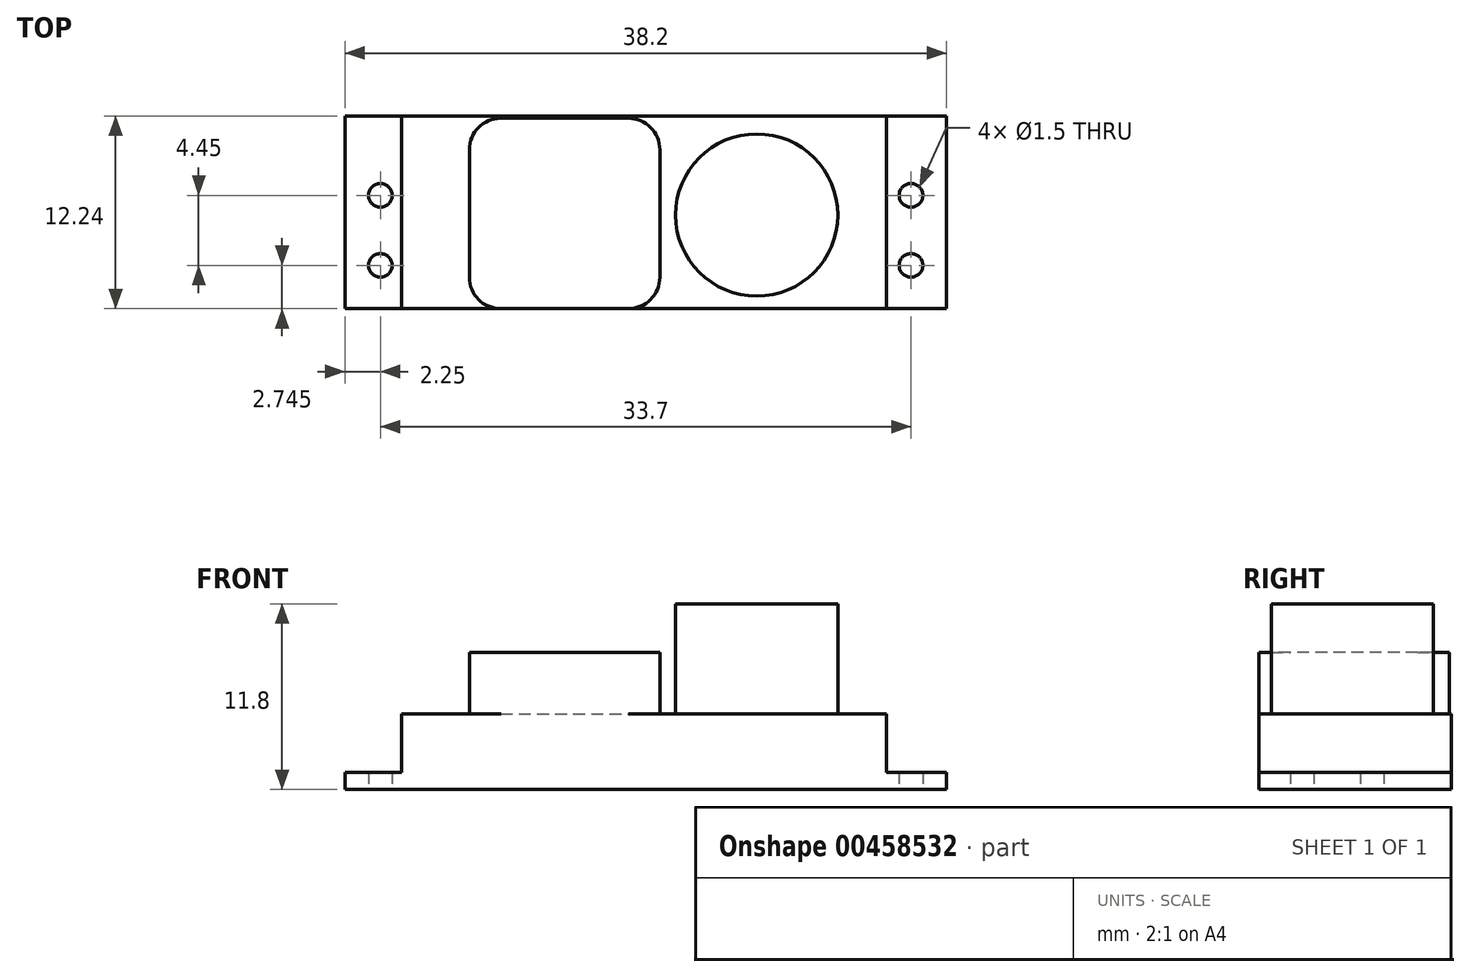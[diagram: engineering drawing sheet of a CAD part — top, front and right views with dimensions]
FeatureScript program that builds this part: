
annotation { "Feature Type Name" : "Feature", "Feature Type Description" : "" }
export const myFeature = defineFeature(function(context is Context, id is Id, definition is map)
    precondition{}
    {
        {
            var Q0;
            Q0=qCreatedBy(makeId("Top.planeOp"),FACE);
            var sketch = newSketch(context, id + "F0", { "sketchPlane" : qUnion([Q0])});
            skLineSegment(sketch, "E0.bottom", {"start": v(-19.1, 6.12) * mm, "end": v(19.1, 6.12) * mm});
            skLineSegment(sketch, "E0.top", {"start": v(-19.1, -6.12) * mm, "end": v(19.1, -6.12) * mm});
            skLineSegment(sketch, "E0.left", {"start": v(-19.1, 6.12) * mm, "end": v(-19.1, -6.12) * mm});
            skLineSegment(sketch, "E0.right", {"start": v(19.1, 6.12) * mm, "end": v(19.1, -6.12) * mm});
            skPoint(sketch, "E0.middle", {"position": v(0, 0) * mm});
            skCircle(sketch, "E1", {"center": v(-16.85, 1.08) * mm, "radius": 0.75 * mm});
            skCircle(sketch, "E2", {"center": v(-16.85, -3.38) * mm, "radius": 0.75 * mm});
            skCircle(sketch, "E3", {"center": v(16.85, 1.08) * mm, "radius": 0.75 * mm});
            skCircle(sketch, "E4", {"center": v(16.85, -3.38) * mm, "radius": 0.75 * mm});
            skSolve(sketch);
        }
        {
            var Q0;
            Q0=qSketchRegion(id+"F0",true);
            extrude(context, id + "F1", {"entities" : qUnion([Q0]), "depth" : 1.1 * mm});
        }
        {
            var Q0;
            Q0=makeQuery(id+"F1.opExtrude","CAP_FACE",FACE,{"disambiguationData":[OSD([sQuery(id+"F0.wireOp",EDGE,"E0.bottom"),sQuery(id+"F0.wireOp",EDGE,"E0.top"),sQuery(id+"F0.wireOp",EDGE,"E0.left"),sQuery(id+"F0.wireOp",EDGE,"E0.right"),sQuery(id+"F0.wireOp",EDGE,"E1"),sQuery(id+"F0.wireOp",EDGE,"E2"),sQuery(id+"F0.wireOp",EDGE,"E3"),sQuery(id+"F0.wireOp",EDGE,"E4")])],"isStart":false});
            var sketch = newSketch(context, id + "F2", { "sketchPlane" : qUnion([Q0])});
            skLineSegment(sketch, "E5", {"start": v(-15.5, 6.12) * mm, "end": v(-15.5, -6.12) * mm});
            skLineSegment(sketch, "E6", {"start": v(15.3, 6.12) * mm, "end": v(15.3, -6.12) * mm});
            skSolve(sketch);
        }
        {
            var Q0;
            {var subQ0=sQuery(id+"F2.wireOp",EDGE,"E5");Q0=makeQuery(id+"F2.imprint","IMPRINT",FACE,{"disambiguationData":[TD([[makeQuery(id+"F2.imprint","IMPRINT",EDGE,{"derivedFrom":subQ0}),1.0]])]});}
            extrude(context, id + "F3", {"entities" : qUnion([Q0]), "operationType" : NewBodyOperationType.ADD, "depth" : 3.7 * mm});
        }
        {
            var Q0;
            Q0=makeQuery(id+"F3.opExtrude","CAP_FACE",FACE,{"disambiguationData":[OSD([sQuery(id+"F0.wireOp",EDGE,"E0.bottom"),sQuery(id+"F0.wireOp",EDGE,"E0.top"),sQuery(id+"F2.wireOp",EDGE,"E5"),sQuery(id+"F2.wireOp",EDGE,"E6")])],"isStart":false});
            var sketch = newSketch(context, id + "F4", { "sketchPlane" : qUnion([Q0])});
            skLineSegment(sketch, "E7.bottom", {"start": v(-9.2, 5.97) * mm, "end": v(-1.1, 5.97) * mm});
            skLineSegment(sketch, "E7.top", {"start": v(-9.2, -6.12) * mm, "end": v(-1.1, -6.12) * mm});
            skLineSegment(sketch, "E7.left", {"start": v(-11.2, 3.97) * mm, "end": v(-11.2, -4.12) * mm});
            skLineSegment(sketch, "E7.right", {"start": v(0.9, 3.97) * mm, "end": v(0.9, -4.12) * mm});
            skCircle(sketch, "E8", {"center": v(7.05, -0.17) * mm, "radius": 5.15 * mm});
            skPoint(sketch, "E9.visualSharp", {"position": v(-11.2, 5.97) * mm});
            skArc(sketch, "E9.filletArc", {"start": v(-9.2, 5.97) * mm, "mid": v(-10.61, 5.39) * mm, "end": v(-11.2, 3.97) * mm});
            skPoint(sketch, "E10.visualSharp", {"position": v(0.9, 5.97) * mm});
            skArc(sketch, "E10.filletArc", {"start": v(0.9, 3.97) * mm, "mid": v(0.31, 5.39) * mm, "end": v(-1.1, 5.97) * mm});
            skPoint(sketch, "E11.visualSharp", {"position": v(0.9, -6.12) * mm});
            skArc(sketch, "E11.filletArc", {"start": v(-1.1, -6.12) * mm, "mid": v(0.31, -5.54) * mm, "end": v(0.9, -4.12) * mm});
            skPoint(sketch, "E12.visualSharp", {"position": v(-11.2, -6.12) * mm});
            skArc(sketch, "E12.filletArc", {"start": v(-11.2, -4.12) * mm, "mid": v(-10.61, -5.54) * mm, "end": v(-9.2, -6.12) * mm});
            skSolve(sketch);
        }
        {
            var Q0;
            Q0=makeQuery(id+"F4.imprint","IMPRINT",FACE,{"disambiguationData":[TD([[makeQuery(id+"F4.imprint","IMPRINT",EDGE,{"derivedFrom":sQuery(id+"F4.wireOp",EDGE,"E7.bottom")}),-1.0]])]});
            extrude(context, id + "F5", {"entities" : qUnion([Q0]), "operationType" : NewBodyOperationType.ADD, "depth" : 3.9 * mm});
        }
        {
            var Q0;
            Q0=makeQuery(id+"F4.imprint","IMPRINT",FACE,{"disambiguationData":[TD([[makeQuery(id+"F4.imprint","IMPRINT",EDGE,{"derivedFrom":sQuery(id+"F4.wireOp",EDGE,"E8")}),1.0]])]});
            extrude(context, id + "F6", {"entities" : qUnion([Q0]), "operationType" : NewBodyOperationType.ADD, "depth" : 7 * mm});
        }
    });
